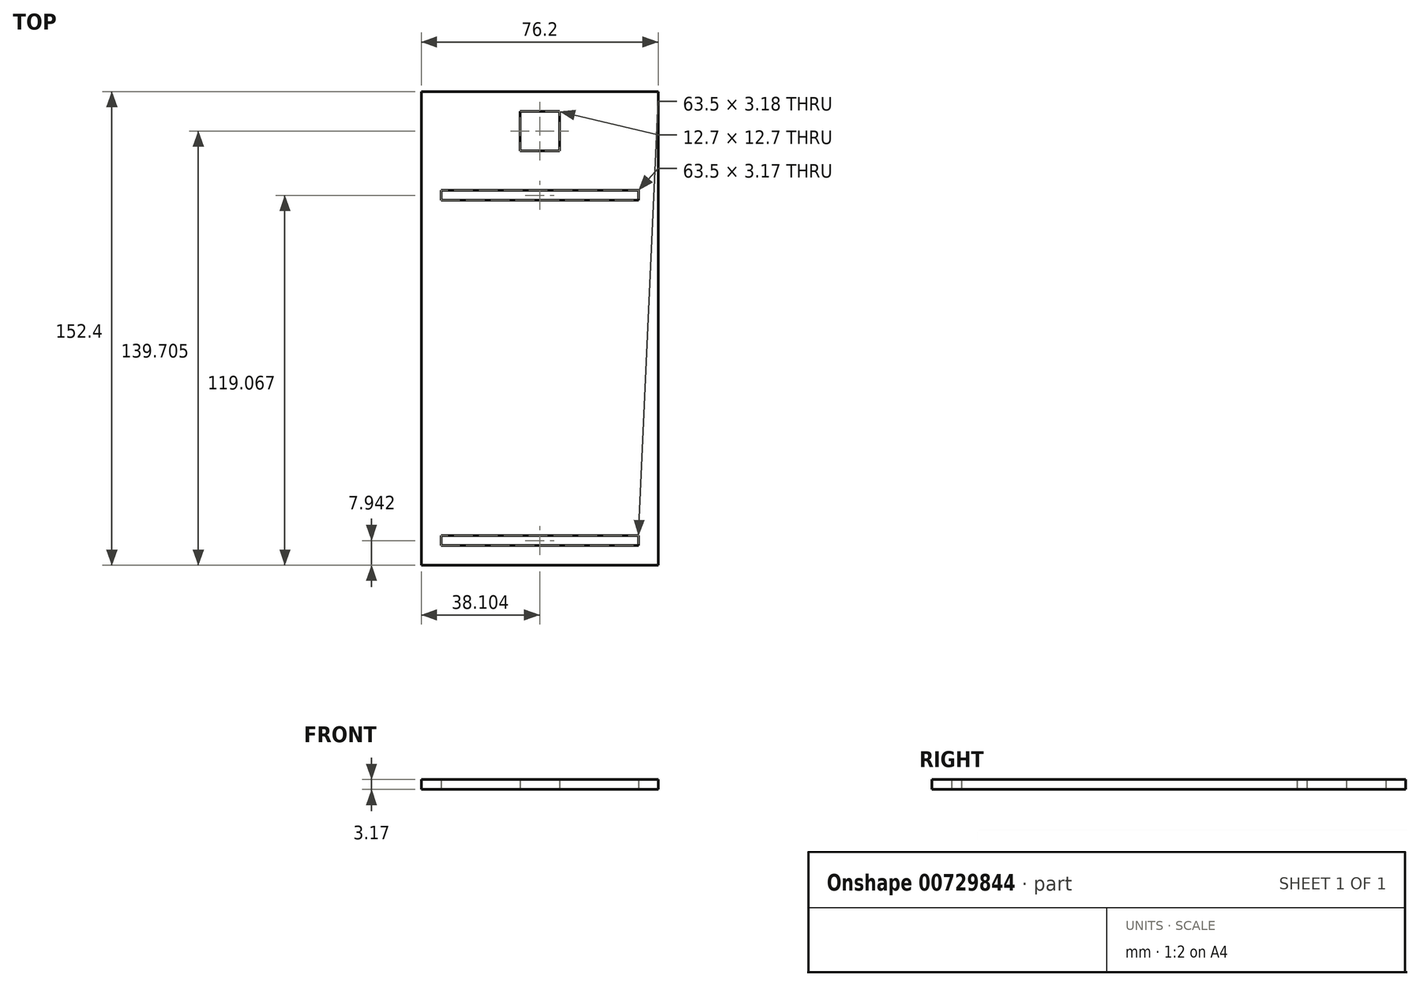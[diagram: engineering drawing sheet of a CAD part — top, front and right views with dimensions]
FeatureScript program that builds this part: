
annotation { "Feature Type Name" : "Feature", "Feature Type Description" : "" }
export const myFeature = defineFeature(function(context is Context, id is Id, definition is map)
    precondition{}
    {
        {
            var Q0;
            Q0=qCreatedBy(makeId("Top.planeOp"),FACE);
            var sketch = newSketch(context, id + "F0", { "sketchPlane" : qUnion([Q0])});
            skLineSegment(sketch, "E0.bottom", {"start": v(-46.54, 117.17) * mm, "end": v(29.66, 117.17) * mm});
            skLineSegment(sketch, "E0.top", {"start": v(-46.54, -9.83) * mm, "end": v(29.66, -9.83) * mm});
            skLineSegment(sketch, "E0.left", {"start": v(-46.54, 117.17) * mm, "end": v(-46.54, -9.83) * mm});
            skLineSegment(sketch, "E0.right", {"start": v(29.66, 117.17) * mm, "end": v(29.66, -9.83) * mm});
            skLineSegment(sketch, "E1.bottom", {"start": v(-46.54, 117.17) * mm, "end": v(-40.19, 117.17) * mm});
            skLineSegment(sketch, "E1.top", {"start": v(-46.54, 110.82) * mm, "end": v(-40.19, 110.82) * mm});
            skLineSegment(sketch, "E1.left", {"start": v(-46.54, 117.17) * mm, "end": v(-46.54, 110.82) * mm});
            skLineSegment(sketch, "E1.right", {"start": v(-40.19, 117.17) * mm, "end": v(-40.19, 110.82) * mm});
            skLineSegment(sketch, "E2.bottom", {"start": v(29.66, 117.17) * mm, "end": v(23.31, 117.17) * mm});
            skLineSegment(sketch, "E2.top", {"start": v(29.66, 110.82) * mm, "end": v(23.31, 110.82) * mm});
            skLineSegment(sketch, "E2.left", {"start": v(29.66, 117.17) * mm, "end": v(29.66, 110.82) * mm});
            skLineSegment(sketch, "E2.right", {"start": v(23.31, 117.17) * mm, "end": v(23.31, 110.82) * mm});
            skLineSegment(sketch, "E3.bottom", {"start": v(-40.19, 110.82) * mm, "end": v(23.31, 110.82) * mm});
            skLineSegment(sketch, "E3.top", {"start": v(-40.19, 107.65) * mm, "end": v(23.31, 107.65) * mm});
            skLineSegment(sketch, "E3.left", {"start": v(-40.19, 110.82) * mm, "end": v(-40.19, 107.65) * mm});
            skLineSegment(sketch, "E3.right", {"start": v(23.31, 110.82) * mm, "end": v(23.31, 107.65) * mm});
            skLineSegment(sketch, "E4.bottom", {"start": v(-46.54, -9.83) * mm, "end": v(-40.19, -9.83) * mm});
            skLineSegment(sketch, "E4.top", {"start": v(-46.54, -3.48) * mm, "end": v(-40.19, -3.48) * mm});
            skLineSegment(sketch, "E4.left", {"start": v(-46.54, -9.83) * mm, "end": v(-46.54, -3.48) * mm});
            skLineSegment(sketch, "E4.right", {"start": v(-40.19, -9.83) * mm, "end": v(-40.19, -3.48) * mm});
            skLineSegment(sketch, "E5.bottom", {"start": v(29.66, -9.83) * mm, "end": v(23.31, -9.83) * mm});
            skLineSegment(sketch, "E5.top", {"start": v(29.66, -3.48) * mm, "end": v(23.31, -3.48) * mm});
            skLineSegment(sketch, "E5.left", {"start": v(29.66, -9.83) * mm, "end": v(29.66, -3.48) * mm});
            skLineSegment(sketch, "E5.right", {"start": v(23.31, -9.83) * mm, "end": v(23.31, -3.48) * mm});
            skLineSegment(sketch, "E6.bottom", {"start": v(23.31, -3.48) * mm, "end": v(-40.19, -3.48) * mm});
            skLineSegment(sketch, "E6.top", {"start": v(23.31, -0.3) * mm, "end": v(-40.19, -0.3) * mm});
            skLineSegment(sketch, "E6.left", {"start": v(23.31, -3.48) * mm, "end": v(23.31, -0.3) * mm});
            skLineSegment(sketch, "E6.right", {"start": v(-40.19, -3.48) * mm, "end": v(-40.19, -0.3) * mm});
            skLineSegment(sketch, "E7.bottom", {"start": v(-46.54, -9.83) * mm, "end": v(4.26, -9.83) * mm});
            skLineSegment(sketch, "E8.top", {"start": v(-46.54, 142.57) * mm, "end": v(29.66, 142.57) * mm});
            skLineSegment(sketch, "E8.left", {"start": v(-46.54, 117.17) * mm, "end": v(-46.54, 142.57) * mm});
            skLineSegment(sketch, "E8.right", {"start": v(29.66, 117.17) * mm, "end": v(29.66, 142.57) * mm});
            skLineSegment(sketch, "E9", {"start": v(29.66, 142.57) * mm, "end": v(-14.79, 142.57) * mm});
            skLineSegment(sketch, "E10", {"start": v(-2.09, 142.57) * mm, "end": v(-14.79, 142.57) * mm});
            skLineSegment(sketch, "E11", {"start": v(-2.09, 142.57) * mm, "end": v(-46.54, 142.57) * mm});
            skLineSegment(sketch, "E12.bottom", {"start": v(-14.79, 142.57) * mm, "end": v(-2.09, 142.57) * mm});
            skLineSegment(sketch, "E12.top", {"start": v(-14.79, 136.22) * mm, "end": v(-2.09, 136.22) * mm});
            skLineSegment(sketch, "E12.left", {"start": v(-2.09, 142.57) * mm, "end": v(-2.09, 136.22) * mm});
            skLineSegment(sketch, "E12.right", {"start": v(-14.79, 142.57) * mm, "end": v(-14.79, 136.22) * mm});
            skLineSegment(sketch, "E13.top", {"start": v(-14.79, 123.52) * mm, "end": v(-2.09, 123.52) * mm});
            skLineSegment(sketch, "E13.left", {"start": v(-2.09, 136.22) * mm, "end": v(-2.09, 123.52) * mm});
            skLineSegment(sketch, "E13.right", {"start": v(-14.79, 136.22) * mm, "end": v(-14.79, 123.52) * mm});
            skSolve(sketch);
        }
        {
            var Q0;
            Q0 = qSketchRegion(id + "F0", true);
            var Q1;
            {var subQ0=sQuery(id+"F0.wireOp",EDGE,"E1.right");Q1=makeQuery(id+"F0.imprint","IMPRINT",FACE,{"disambiguationData":[TD([[makeQuery(id+"F0.imprint","IMPRINT",EDGE,{"derivedFrom":subQ0}),1.0]])]});}
            extrude(context, id + "F1", {"entities" : qUnion([Q0, Q1]), "depth" : 3.17 * mm, "offsetDistance" : 25.4 * mm});
        }
    });
